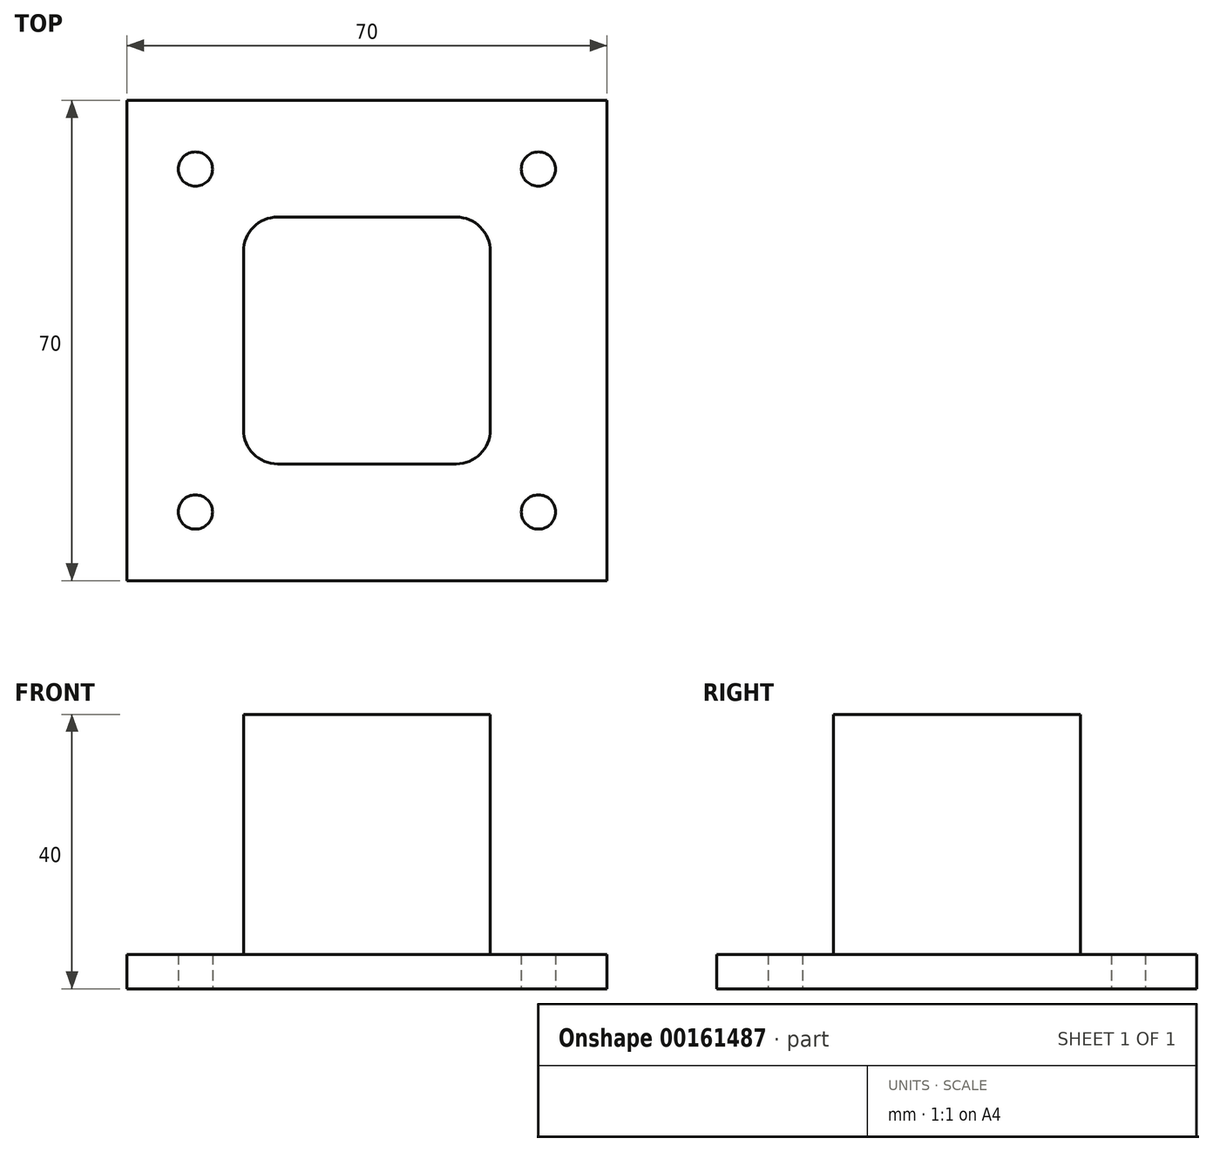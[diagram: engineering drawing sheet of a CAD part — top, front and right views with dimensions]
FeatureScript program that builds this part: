
annotation { "Feature Type Name" : "Feature", "Feature Type Description" : "" }
export const myFeature = defineFeature(function(context is Context, id is Id, definition is map)
    precondition{}
    {
        {
            var Q0;
            Q0=qCreatedBy(makeId("Top.planeOp"),FACE);
            var sketch = newSketch(context, id + "F0", { "sketchPlane" : qUnion([Q0])});
            skLineSegment(sketch, "E0.bottom", {"start": v(35, -35) * mm, "end": v(-35, -35) * mm});
            skLineSegment(sketch, "E0.top", {"start": v(35, 35) * mm, "end": v(-35, 35) * mm});
            skLineSegment(sketch, "E0.left", {"start": v(35, -35) * mm, "end": v(35, 35) * mm});
            skLineSegment(sketch, "E0.right", {"start": v(-35, -35) * mm, "end": v(-35, 35) * mm});
            skPoint(sketch, "E0.middle", {"position": v(0, 0) * mm});
            skPoint(sketch, "E1", {"position": v(-25, 25) * mm});
            skPoint(sketch, "E2.MirrorP", {"position": v(25, 25) * mm});
            skPoint(sketch, "E3.MirrorP", {"position": v(25, -25) * mm});
            skPoint(sketch, "E4.MirrorP", {"position": v(-25, -25) * mm});
            skSolve(sketch);
        }
        {
            var Q0;
            Q0 = qSketchRegion(id + "F0", true);
            extrude(context, id + "F1", {"entities" : qUnion([Q0]), "depth" : 5 * mm, "offsetDistance" : 25 * mm});
        }
        {
            var Q0;
            Q0=sQuery(id+"F0.wireOp",VERTEX,"E1");
            var Q1;
            Q1=sQuery(id+"F0.wireOp",VERTEX,"10a93406-9afa-4daa-8156-0129914206ab.1.0.0");
            var Q2;
            Q2=sQuery(id+"F0.wireOp",VERTEX,"10a93406-9afa-4daa-8156-0129914206ab.2.0.0");
            var Q3;
            Q3=sQuery(id+"F0.wireOp",VERTEX,"10a93406-9afa-4daa-8156-0129914206ab.3.0.0");
            var Q4;
            Q4=sQuery(id+"F0.wireOp",VERTEX,"731a2151-4463-44e7-8b94-e1bdc1e52f1c0.MirrorP");
            var Q5;
            Q5=sQuery(id+"F0.wireOp",VERTEX,"731a2151-4463-44e7-8b94-e1bdc1e52f1c1.MirrorP");
            var Q6;
            Q6=sQuery(id+"F0.wireOp",VERTEX,"731a2151-4463-44e7-8b94-e1bdc1e52f1c2.MirrorP");
            var Q7;
            Q7=sQuery(id+"F0.wireOp",VERTEX,"731a2151-4463-44e7-8b94-e1bdc1e52f1c3.MirrorP");
            var Q8;
            Q8=sQuery(id+"F0.wireOp",VERTEX,"E2.MirrorP");
            var Q9;
            Q9=sQuery(id+"F0.wireOp",VERTEX,"E3.MirrorP");
            var Q10;
            Q10=sQuery(id+"F0.wireOp",VERTEX,"E4.MirrorP");
            var Q11;
            Q11=makeQuery(id+"F1.opExtrude","SWEPT_BODY",BODY,{"disambiguationData":[OSD([sQuery(id+"F0.wireOp",EDGE,"E0.bottom"),sQuery(id+"F0.wireOp",EDGE,"E0.top"),sQuery(id+"F0.wireOp",EDGE,"E0.left"),sQuery(id+"F0.wireOp",EDGE,"E0.right")])]});
            hole(context, id + "F2", {"style" : HoleStyle.SIMPLE, "endStyle" : HoleEndStyle.THROUGH, "oppositeDirection" : true, "holeDiameter" : 5 * mm, "majorDiameter" : 5 * mm, "isTappedThrough" : true, "tappedDepth" : 12 * mm, "tapClearance" : 3, "locations" : qUnion([Q0, Q1, Q2, Q3, Q4, Q5, Q6, Q7, Q8, Q9, Q10]), "scope" : qUnion([Q11])});
        }
        {
            var Q0;
            Q0=makeQuery(id+"F1.opExtrude","CAP_FACE",FACE,{"disambiguationData":[OSD([sQuery(id+"F0.wireOp",EDGE,"E0.bottom"),sQuery(id+"F0.wireOp",EDGE,"E0.top"),sQuery(id+"F0.wireOp",EDGE,"E0.left"),sQuery(id+"F0.wireOp",EDGE,"E0.right")])],"isStart":false});
            var sketch = newSketch(context, id + "F3", { "sketchPlane" : qUnion([Q0])});
            skLineSegment(sketch, "E5.bottom", {"start": v(18, -18) * mm, "end": v(-18, -18) * mm});
            skLineSegment(sketch, "E5.top", {"start": v(18, 18) * mm, "end": v(-18, 18) * mm});
            skLineSegment(sketch, "E5.left", {"start": v(18, -18) * mm, "end": v(18, 18) * mm});
            skLineSegment(sketch, "E5.right", {"start": v(-18, -18) * mm, "end": v(-18, 18) * mm});
            skPoint(sketch, "E5.middle", {"position": v(0, 0) * mm});
            skSolve(sketch);
        }
        {
            var Q0;
            Q0 = qSketchRegion(id + "F3", true);
            extrude(context, id + "F4", {"entities" : qUnion([Q0]), "operationType" : NewBodyOperationType.ADD, "depth" : 35 * mm, "offsetDistance" : 25 * mm});
        }
        {
            var Q0;
            Q0=makeQuery(id+"F4.opExtrude","SWEPT_EDGE",EDGE,{"disambiguationData":[OSD([sQuery(id+"F3.wireOp",EDGE,"E5.top"),sQuery(id+"F3.wireOp",EDGE,"E5.right")])]});
            var Q1;
            Q1=makeQuery(id+"F4.opExtrude","SWEPT_EDGE",EDGE,{"disambiguationData":[OSD([sQuery(id+"F3.wireOp",EDGE,"E5.bottom"),sQuery(id+"F3.wireOp",EDGE,"E5.right")])]});
            var Q2;
            Q2=makeQuery(id+"F4.opExtrude","SWEPT_EDGE",EDGE,{"disambiguationData":[OSD([sQuery(id+"F3.wireOp",EDGE,"E5.bottom"),sQuery(id+"F3.wireOp",EDGE,"E5.left")])]});
            var Q3;
            Q3=makeQuery(id+"F4.opExtrude","SWEPT_EDGE",EDGE,{"disambiguationData":[OSD([sQuery(id+"F3.wireOp",EDGE,"E5.top"),sQuery(id+"F3.wireOp",EDGE,"E5.left")])]});
            fillet(context, id + "F5", {"entities" : qUnion([Q0, Q1, Q2, Q3]), "radius" : 5 * mm, "tangentPropagation" : true, "allowEdgeOverflow" : false});
        }
    });
